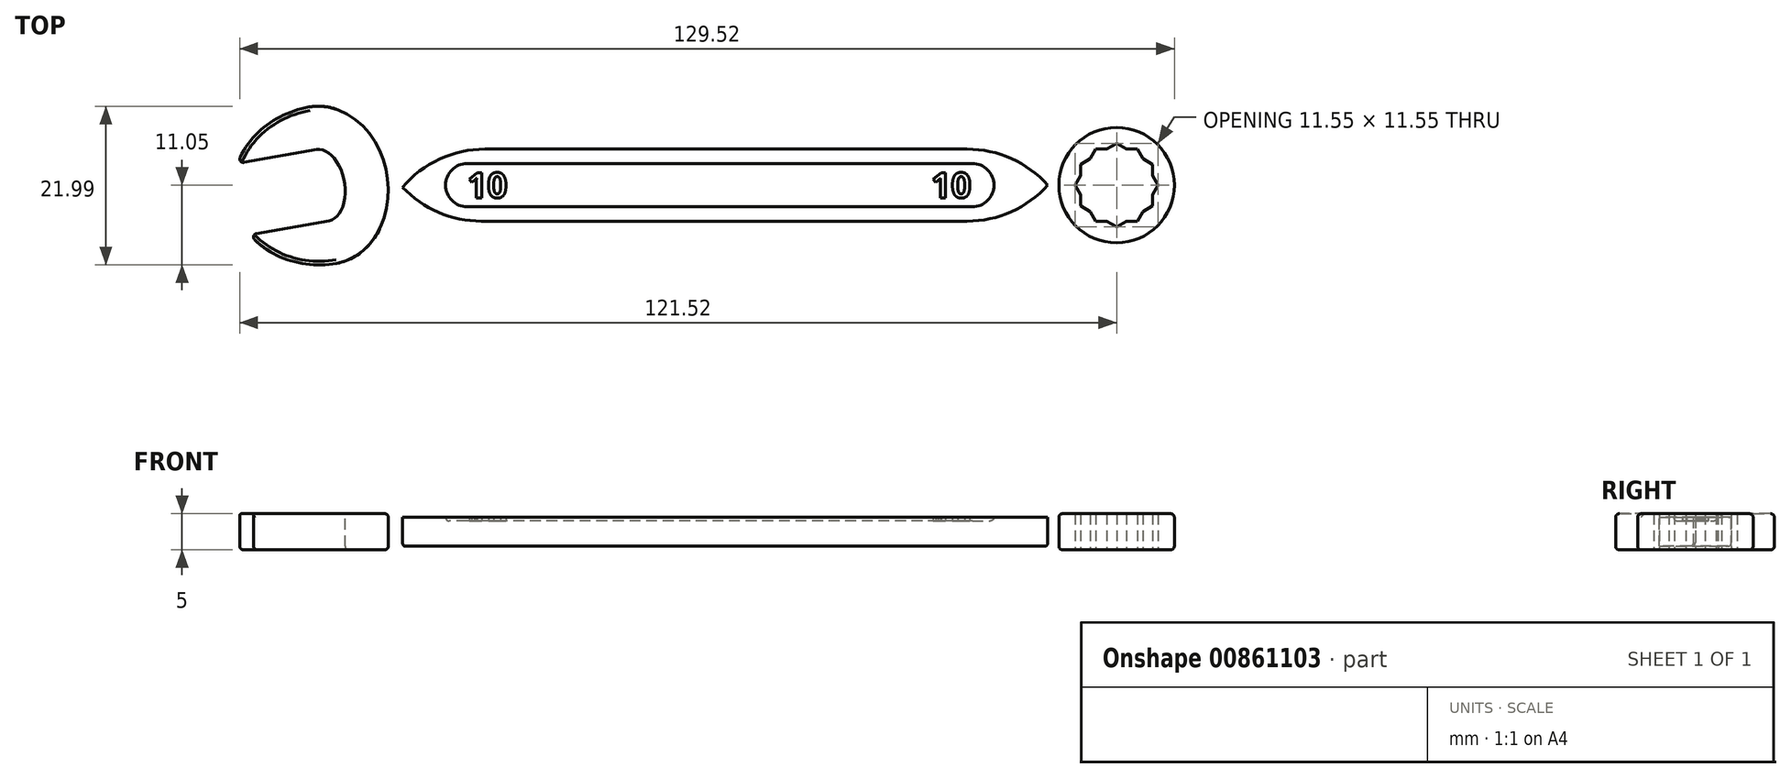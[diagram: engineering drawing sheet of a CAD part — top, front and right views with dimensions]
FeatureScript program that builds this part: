
annotation { "Feature Type Name" : "Feature", "Feature Type Description" : "" }
export const myFeature = defineFeature(function(context is Context, id is Id, definition is map)
    precondition{}
    {
        {
            assignVariable(context, id + "F0", {"name" : "AF", "anyValue" : 10});
        }
        {
            var Q0;
            Q0=qCreatedBy(makeId("Top.planeOp"),FACE);
            var sketch = newSketch(context, id + "F1", { "sketchPlane" : qUnion([Q0])});
            skArc(sketch, "E0.cCircle", {"start": v(50.67, -2.5) * mm, "mid": v(60, 0) * mm, "end": v(50.67, 2.5) * mm, "construction": true});
            skLineSegment(sketch, "E0.0", {"start": v(60, 2.89) * mm, "end": v(60, 1.34) * mm});
            skLineSegment(sketch, "E0.1", {"start": v(60, -2.89) * mm, "end": v(58.66, -3.66) * mm});
            skLineSegment(sketch, "E0.2", {"start": v(55, -5.77) * mm, "end": v(53.66, -5) * mm});
            skLineSegment(sketch, "E0.3", {"start": v(50, -2.89) * mm, "end": v(50, -1.34) * mm});
            skLineSegment(sketch, "E0.4", {"start": v(50, 2.89) * mm, "end": v(51.34, 3.66) * mm});
            skLineSegment(sketch, "E0.5", {"start": v(55, 5.77) * mm, "end": v(56.34, 5) * mm});
            skPoint(sketch, "E0.0.midPoint", {"position": v(60, 0) * mm});
            skCircle(sketch, "E1.cCircle", {"center": v(55, 0) * mm, "radius": 5 * mm, "construction": true});
            skLineSegment(sketch, "E1.0", {"start": v(57.89, -5) * mm, "end": v(56.34, -5) * mm});
            skLineSegment(sketch, "E1.1", {"start": v(52.11, -5) * mm, "end": v(51.34, -3.66) * mm});
            skLineSegment(sketch, "E1.2", {"start": v(49.23, 0) * mm, "end": v(50, 1.34) * mm});
            skLineSegment(sketch, "E1.3", {"start": v(52.11, 5) * mm, "end": v(53.66, 5) * mm});
            skLineSegment(sketch, "E1.4", {"start": v(57.89, 5) * mm, "end": v(58.66, 3.66) * mm});
            skLineSegment(sketch, "E1.5", {"start": v(60.77, 0) * mm, "end": v(60, -1.34) * mm});
            skPoint(sketch, "E1.0.midPoint", {"position": v(55, -5) * mm});
            skCircle(sketch, "E2", {"center": v(55, 0) * mm, "radius": 8 * mm});
            skLineSegment(sketch, "E3.trimOffspring", {"start": v(50, -1.34) * mm, "end": v(49.23, 0) * mm});
            skLineSegment(sketch, "E4.trimOffspring", {"start": v(50, 1.34) * mm, "end": v(50, 2.89) * mm});
            skLineSegment(sketch, "E5.trimOffspring", {"start": v(51.34, 3.66) * mm, "end": v(52.11, 5) * mm});
            skLineSegment(sketch, "E6.trimOffspring", {"start": v(53.66, 5) * mm, "end": v(55, 5.77) * mm});
            skLineSegment(sketch, "E7.trimOffspring", {"start": v(56.34, 5) * mm, "end": v(57.89, 5) * mm});
            skLineSegment(sketch, "E8.trimOffspring", {"start": v(58.66, 3.66) * mm, "end": v(60, 2.89) * mm});
            skLineSegment(sketch, "E9.trimOffspring", {"start": v(60, 1.34) * mm, "end": v(60.77, 0) * mm});
            skLineSegment(sketch, "E10.trimOffspring", {"start": v(60, -1.34) * mm, "end": v(60, -2.89) * mm});
            skLineSegment(sketch, "E11.trimOffspring", {"start": v(58.66, -3.66) * mm, "end": v(57.89, -5) * mm});
            skLineSegment(sketch, "E12.trimOffspring", {"start": v(56.34, -5) * mm, "end": v(55, -5.77) * mm});
            skLineSegment(sketch, "E13.trimOffspring", {"start": v(51.34, -3.66) * mm, "end": v(50, -2.89) * mm});
            skLineSegment(sketch, "E14.trimOffspring", {"start": v(53.66, -5) * mm, "end": v(52.11, -5) * mm});
            skLineSegment(sketch, "E15", {"start": v(-55, 0) * mm, "end": v(-55, 16.24) * mm, "construction": true});
            skLineSegment(sketch, "E16", {"start": v(-55, 0) * mm, "end": v(-56.91, 10.83) * mm, "construction": true});
            skEllipticalArc(sketch, "E17", {});
            skEllipticalArc(sketch, "E18", {});
            skLineSegment(sketch, "E19", {"start": v(-55, 0) * mm, "end": v(-54.13, -4.92) * mm, "construction": true});
            skEllipticalArc(sketch, "E20", {});
            skLineSegment(sketch, "E21", {"start": v(-55.87, 4.92) * mm, "end": v(-66.83, 3) * mm});
            skLineSegment(sketch, "E22", {"start": v(-54.13, -4.92) * mm, "end": v(-65.1, -6.86) * mm});
            skEllipticalArc(sketch, "E23.trimOffspring", {});
            const initialGuessF1  = {"E17": [-0.055, 0, -0.1736481776669304, 0.984807753012208, 0.011, 0.009, 3.141592653589793, 0], "E18": [-0.055, 0, -0.17364817766693033, 0.9848077530122081, 0.011, 0.0125, 2.0426581640745396, 3.141592653589793], "E20": [-0.055, 0, 0.17364817766693058, -0.984807753012208, 0.005, 0.003, 0, 3.1415926535897936], "E23.trimOffspring": [-0.055, 0, -0.1736481776669303, 0.9848077530122081, 0.011, 0.0125, 6.129245203673409, 1.0989344895152549]};
            skSetInitialGuess(sketch, initialGuessF1);
            skSolve(sketch);
        }
        {
            var Q0;
            Q0=qCreatedBy(makeId("Right.planeOp"),FACE);
            var sketch = newSketch(context, id + "F2", { "sketchPlane" : qUnion([Q0])});
            skLineSegment(sketch, "E24.bottom", {"start": v(-5, 2) * mm, "end": v(5, 2) * mm});
            skLineSegment(sketch, "E24.top", {"start": v(-5, -2) * mm, "end": v(5, -2) * mm});
            skLineSegment(sketch, "E24.left", {"start": v(-5, 2) * mm, "end": v(-5, -2) * mm});
            skLineSegment(sketch, "E24.right", {"start": v(5, 2) * mm, "end": v(5, -2) * mm});
            skPoint(sketch, "E24.middle", {"position": v(0, 0) * mm});
            skSolve(sketch);
        }
        {
            var Q0;
            Q0 = qSketchRegion(id + "F1", true);
            extrude(context, id + "F3", {"entities" : qUnion([Q0]), "endBound" : BoundingType.SYMMETRIC, "depth" : (getVariable(context, 'AF') * 0.5) * mm, "offsetDistance" : 25 * mm});
        }
        {
            var Q0;
            Q0 = qSketchRegion(id + "F2", true);
            var Q1;
            Q1=makeQuery(id+"F3.opExtrude","SWEPT_FACE",FACE,{"disambiguationData":[OSD([sQuery(id+"F1.wireOp",EDGE,"E2")])]});
            var Q2;
            Q2=makeQuery(id+"F3.opExtrude","SWEPT_FACE",FACE,{"disambiguationData":[OSD([sQuery(id+"F1.wireOp",EDGE,"E17")])]});
            extrude(context, id + "F4", {"entities" : qUnion([Q0]), "endBound" : BoundingType.UP_TO_SURFACE, "depth" : 25 * mm, "endBoundEntityFace" : qUnion([Q1]), "offsetDistance" : 25 * mm, "hasSecondDirection" : true, "secondDirectionBound" : SecondDirectionBoundingType.UP_TO_SURFACE, "secondDirectionOppositeDirection" : true, "secondDirectionDepth" : 25 * mm, "secondDirectionBoundEntityFace" : qUnion([Q2])});
        }
        {
            var Q0;
            Q0=makeQuery(id+"F4.opExtrude","SWEPT_FACE",FACE,{"disambiguationData":[OSD([sQuery(id+"F2.wireOp",EDGE,"E24.bottom")])]});
            var sketch = newSketch(context, id + "F5", { "sketchPlane" : qUnion([Q0])});
            skLineSegment(sketch, "E25.bottom", {"start": v(35, 3) * mm, "end": v(-35, 3) * mm});
            skLineSegment(sketch, "E25.top", {"start": v(35, -3) * mm, "end": v(-35, -3) * mm});
            skPoint(sketch, "E25.middle", {"position": v(0, 0) * mm});
            skArc(sketch, "E26", {"start": v(-35, 3) * mm, "mid": v(-38, 0) * mm, "end": v(-35, -3) * mm});
            skArc(sketch, "E27", {"start": v(35, -3) * mm, "mid": v(38, 0) * mm, "end": v(35, 3) * mm});
            skSolve(sketch);
        }
        {
            var Q0;
            Q0 = qSketchRegion(id + "F5", true);
            extrude(context, id + "F6", {"entities" : qUnion([Q0]), "operationType" : NewBodyOperationType.REMOVE, "oppositeDirection" : true, "depth" : .5 * mm, "offsetDistance" : 25 * mm});
        }
        {
            var Q0;
            Q0=makeQuery(id+"F6.boolean.opBoolean","COPY",FACE,{"derivedFrom":makeQuery(id+"F6.opExtrude","CAP_FACE",FACE,{"disambiguationData":[OSD([sQuery(id+"F5.wireOp",EDGE,"E25.bottom"),sQuery(id+"F5.wireOp",EDGE,"E25.top"),sQuery(id+"F5.wireOp",EDGE,"E26"),sQuery(id+"F5.wireOp",EDGE,"E27")])],"isStart":false})});
            var sketch = newSketch(context, id + "F7", { "sketchPlane" : qUnion([Q0])});
            skText(sketch, "E28", { "text": "10", "fontName": "OpenSans-Bold.ttf"});
            skText(sketch, "E29", { "text": "10", "fontName": "OpenSans-Bold.ttf"});
            const initialGuessF7  = {"E28": [-0.035, -0.00175, 1, 0, 0.0035], "E29": [0.0293, -0.00175, 1, 0, 0.0035]};
            skSetInitialGuess(sketch, initialGuessF7);
            skSolve(sketch);
        }
        {
            var Q0;
            Q0 = qSketchRegion(id + "F7", true);
            extrude(context, id + "F8", {"entities" : qUnion([Q0]), "operationType" : NewBodyOperationType.ADD, "depth" : .5 * mm, "offsetDistance" : 25 * mm});
        }
        {
            var Q0;
            Q0=makeQuery(id+"F4.opExtrude","CAP_EDGE",EDGE,{"disambiguationData":[OSD([sQuery(id+"F2.wireOp",EDGE,"E24.left")]),topologyDisambiguationEdgeConnected([makeQuery(id+"F3.opExtrude","SWEPT_FACE",FACE,{"disambiguationData":[OSD([sQuery(id+"F1.wireOp",EDGE,"E2")])]})])],"isStart":false});
            var Q1;
            Q1=makeQuery(id+"F4.opExtrude","CAP_EDGE",EDGE,{"disambiguationData":[OSD([sQuery(id+"F2.wireOp",EDGE,"E24.right")]),topologyDisambiguationEdgeConnected([makeQuery(id+"F3.opExtrude","SWEPT_FACE",FACE,{"disambiguationData":[OSD([sQuery(id+"F1.wireOp",EDGE,"E2")])]})])],"isStart":false});
            var Q2;
            Q2=makeQuery(id+"F4.opExtrude","CAP_EDGE",EDGE,{"disambiguationData":[OSD([sQuery(id+"F2.wireOp",EDGE,"E24.left")]),topologyDisambiguationEdgeConnected([makeQuery(id+"F3.opExtrude","SWEPT_FACE",FACE,{"disambiguationData":[OSD([sQuery(id+"F1.wireOp",EDGE,"E17")])]})])],"isStart":false});
            var Q3;
            Q3=makeQuery(id+"F4.opExtrude","CAP_EDGE",EDGE,{"disambiguationData":[OSD([sQuery(id+"F2.wireOp",EDGE,"E24.right")]),topologyDisambiguationEdgeConnected([makeQuery(id+"F3.opExtrude","SWEPT_FACE",FACE,{"disambiguationData":[OSD([sQuery(id+"F1.wireOp",EDGE,"E17")])]})])],"isStart":false});
            fillet(context, id + "F9", {"entities" : qUnion([Q0, Q1, Q2, Q3]), "radius" : (getVariable(context, 'AF') * 1.5) * mm, "tangentPropagation" : true, "allowEdgeOverflow" : false});
        }
        {
            var Q0;
            Q0=makeQuery(id+"F4.opExtrude","TWEAK_EDGE",EDGE,{"derivedFrom":[makeQuery(id+"F2.imprint","IMPRINT",EDGE,{"derivedFrom":sQuery(id+"F2.wireOp",EDGE,"E24.bottom")}),makeQuery(id+"F2.imprint","IMPRINT",EDGE,{"derivedFrom":sQuery(id+"F2.wireOp",EDGE,"E24.left")})]});
            var Q1;
            Q1=makeQuery(id+"F6.boolean.opBoolean","COPY",EDGE,{"derivedFrom":makeQuery(id+"F6.opExtrude","CAP_EDGE",EDGE,{"disambiguationData":[OSD([sQuery(id+"F5.wireOp",EDGE,"E25.bottom")])],"isStart":false})});
            var Q2;
            Q2=makeQuery(id+"F4.opExtrude","TWEAK_EDGE",EDGE,{"derivedFrom":[makeQuery(id+"F2.imprint","IMPRINT",EDGE,{"derivedFrom":sQuery(id+"F2.wireOp",EDGE,"E24.bottom")}),makeQuery(id+"F2.imprint","IMPRINT",EDGE,{"derivedFrom":sQuery(id+"F2.wireOp",EDGE,"E24.right")})]});
            var Q3;
            Q3=makeQuery(id+"F3.opExtrude","CAP_EDGE",EDGE,{"disambiguationData":[OSD([sQuery(id+"F1.wireOp",EDGE,"E2")])],"isStart":false});
            var Q4;
            Q4=makeQuery(id+"F3.opExtrude","CAP_EDGE",EDGE,{"disambiguationData":[OSD([sQuery(id+"F1.wireOp",EDGE,"E23.trimOffspring")])],"isStart":false});
            var Q5;
            Q5=makeQuery(id+"F3.opExtrude","SWEPT_EDGE",EDGE,{"disambiguationData":[OSD([sQuery(id+"F1.wireOp",EDGE,"E21"),sQuery(id+"F1.wireOp",EDGE,"E23.trimOffspring")])]});
            var Q6;
            Q6=makeQuery(id+"F3.opExtrude","SWEPT_EDGE",EDGE,{"disambiguationData":[OSD([sQuery(id+"F1.wireOp",EDGE,"E18"),sQuery(id+"F1.wireOp",EDGE,"E22")])]});
            fillet(context, id + "F10", {"entities" : qUnion([Q0, Q1, Q2, Q3, Q4, Q5, Q6]), "radius" : (getVariable(context, 'AF') * 0.05) * mm, "tangentPropagation" : true, "allowEdgeOverflow" : false});
        }
        {
            var Q0;
            Q0=makeQuery(id+"F3.opExtrude","CAP_EDGE",EDGE,{"disambiguationData":[OSD([sQuery(id+"F1.wireOp",EDGE,"E23.trimOffspring")])],"isStart":true});
            var Q1;
            Q1=makeQuery(id+"F9.opFillet","BLEND_EDGE",EDGE,{"blendedFrom":[makeQuery(id+"F4.opExtrude","CAP_EDGE",EDGE,{"disambiguationData":[OSD([sQuery(id+"F2.wireOp",EDGE,"E24.right")]),topologyDisambiguationEdgeConnected([makeQuery(id+"F3.opExtrude","SWEPT_FACE",FACE,{"disambiguationData":[OSD([sQuery(id+"F1.wireOp",EDGE,"E17")])]})])],"isStart":false}),makeQuery(id+"F4.opExtrude","SWEPT_FACE",FACE,{"disambiguationData":[OSD([sQuery(id+"F2.wireOp",EDGE,"E24.top")])]})],"blendedInto":[makeQuery(id+"F4.opExtrude","SWEPT_FACE",FACE,{"disambiguationData":[OSD([sQuery(id+"F2.wireOp",EDGE,"E24.top")])]})]});
            var Q2;
            Q2=makeQuery(id+"F3.opExtrude","CAP_EDGE",EDGE,{"disambiguationData":[OSD([sQuery(id+"F1.wireOp",EDGE,"E2")])],"isStart":true});
            var Q3;
            Q3=makeQuery(id+"F4.opExtrude","TWEAK_EDGE",EDGE,{"derivedFrom":[makeQuery(id+"F2.imprint","IMPRINT",EDGE,{"derivedFrom":sQuery(id+"F2.wireOp",EDGE,"E24.top")}),makeQuery(id+"F2.imprint","IMPRINT",EDGE,{"derivedFrom":sQuery(id+"F2.wireOp",EDGE,"E24.left")})]});
            fillet(context, id + "F11", {"entities" : qUnion([Q0, Q1, Q2, Q3]), "radius" : (getVariable(context, 'AF') * 0.05) * mm, "tangentPropagation" : true, "allowEdgeOverflow" : false});
        }
    });
